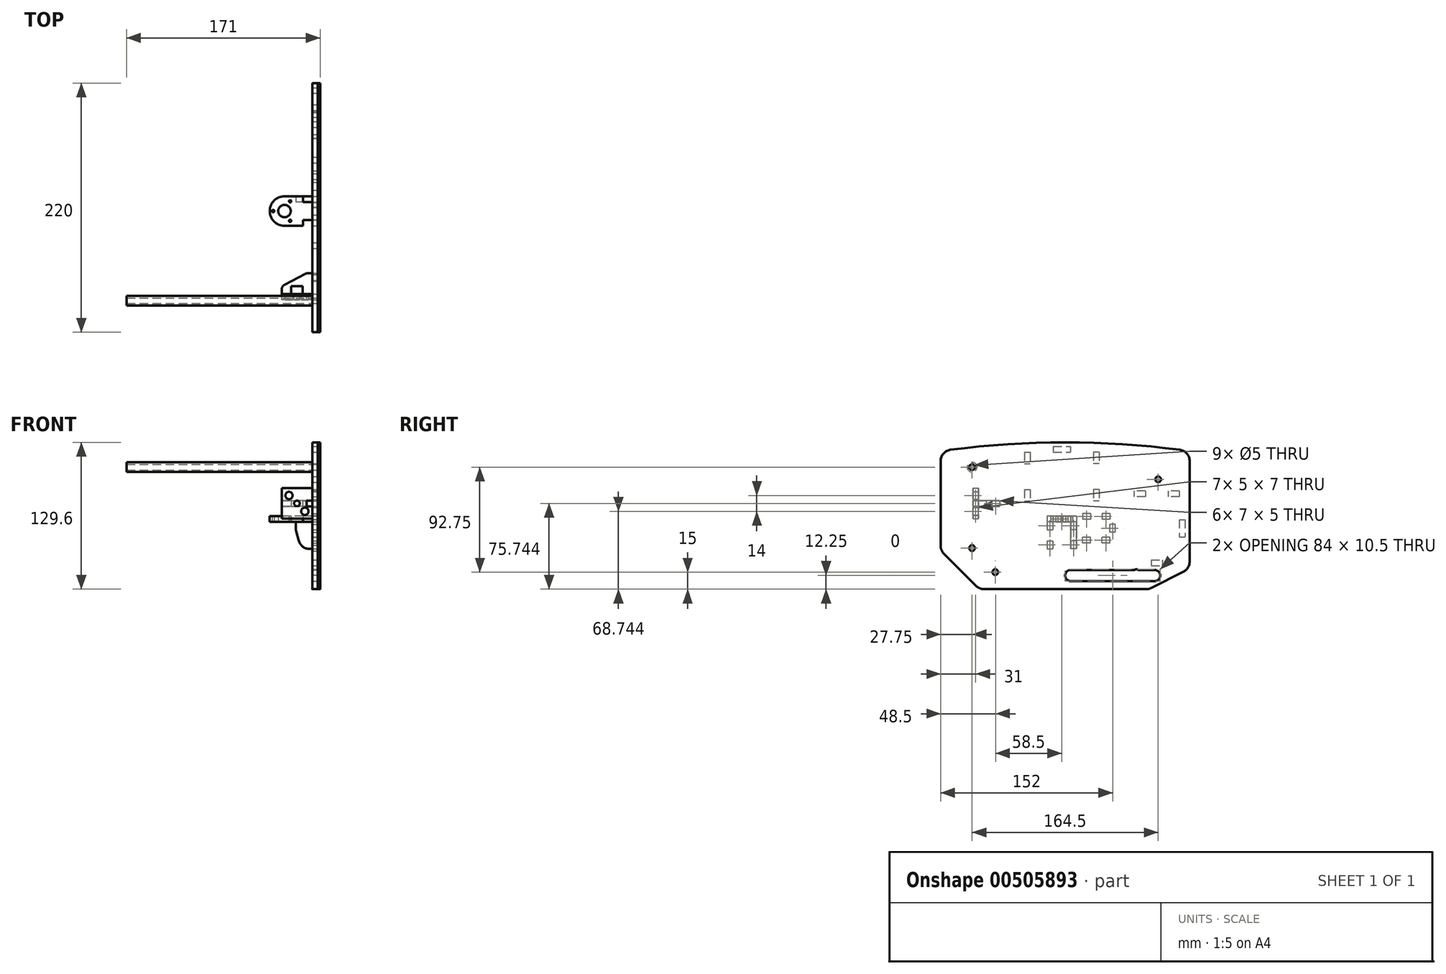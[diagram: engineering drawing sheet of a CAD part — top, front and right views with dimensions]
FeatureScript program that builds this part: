
annotation { "Feature Type Name" : "Feature", "Feature Type Description" : "" }
export const myFeature = defineFeature(function(context is Context, id is Id, definition is map)
    precondition{}
    {
        {
            var Q0;
            Q0=qCreatedBy(makeId("Right.planeOp"),FACE);
            var sketch = newSketch(context, id + "F0", { "sketchPlane" : qUnion([Q0])});
            skLineSegment(sketch, "E0", {"start": v(-71.74, 0) * mm, "end": v(71.74, 0) * mm});
            skLineSegment(sketch, "E1", {"start": v(-78.81, 2.93) * mm, "end": v(-107.07, 31.17) * mm});
            skLineSegment(sketch, "E2", {"start": v(-110, 38.24) * mm, "end": v(-110, 113.24) * mm});
            skLineSegment(sketch, "E3", {"start": v(76.24, 1.07) * mm, "end": v(104.5, 15.31) * mm});
            skLineSegment(sketch, "E4", {"start": v(110, 24.24) * mm, "end": v(110, 113.24) * mm});
            skArc(sketch, "E5", {"start": v(-101.27, 123.16) * mm, "mid": v(0, 129.6) * mm, "end": v(101.27, 123.16) * mm});
            skPoint(sketch, "E6.visualSharp", {"position": v(-110, 122) * mm});
            skArc(sketch, "E6.filletArc", {"start": v(-101.27, 123.16) * mm, "mid": v(-107.5, 119.85) * mm, "end": v(-110, 113.24) * mm});
            skPoint(sketch, "E7.visualSharp", {"position": v(-110, 34.1) * mm});
            skArc(sketch, "E7.filletArc", {"start": v(-110, 38.24) * mm, "mid": v(-109.24, 34.42) * mm, "end": v(-107.07, 31.17) * mm});
            skPoint(sketch, "E8.visualSharp", {"position": v(-75.88, 0) * mm});
            skArc(sketch, "E8.filletArc", {"start": v(-78.81, 2.93) * mm, "mid": v(-75.57, 0.76) * mm, "end": v(-71.74, 0) * mm});
            skPoint(sketch, "E9.visualSharp", {"position": v(74.12, 0) * mm});
            skArc(sketch, "E9.filletArc", {"start": v(71.74, 0) * mm, "mid": v(74.05, 0.27) * mm, "end": v(76.24, 1.07) * mm});
            skPoint(sketch, "E10.visualSharp", {"position": v(110, 18.09) * mm});
            skArc(sketch, "E10.filletArc", {"start": v(104.5, 15.31) * mm, "mid": v(108.51, 19) * mm, "end": v(110, 24.24) * mm});
            skPoint(sketch, "E11.visualSharp", {"position": v(110, 122) * mm});
            skArc(sketch, "E11.filletArc", {"start": v(110, 113.24) * mm, "mid": v(107.5, 119.85) * mm, "end": v(101.27, 123.16) * mm});
            skSolve(sketch);
        }
        {
            var Q0;
            Q0 = qSketchRegion(id + "F0", true);
            extrude(context, id + "F1", {"entities" : qUnion([Q0]), "depth" : 5 * mm});
        }
        {
            var Q0;
            Q0=makeQuery(id+"F1.opExtrude","CAP_FACE",FACE,{"disambiguationData":[OSD([sQuery(id+"F0.wireOp",EDGE,"E0"),sQuery(id+"F0.wireOp",EDGE,"E1"),sQuery(id+"F0.wireOp",EDGE,"E2"),sQuery(id+"F0.wireOp",EDGE,"E3"),sQuery(id+"F0.wireOp",EDGE,"E4"),sQuery(id+"F0.wireOp",EDGE,"E5"),sQuery(id+"F0.wireOp",EDGE,"E6.filletArc"),sQuery(id+"F0.wireOp",EDGE,"E7.filletArc"),sQuery(id+"F0.wireOp",EDGE,"E8.filletArc"),sQuery(id+"F0.wireOp",EDGE,"E9.filletArc"),sQuery(id+"F0.wireOp",EDGE,"E10.filletArc"),sQuery(id+"F0.wireOp",EDGE,"E11.filletArc")])],"isStart":false});
            var sketch = newSketch(context, id + "F2", { "sketchPlane" : qUnion([Q0])});
            skLineSegment(sketch, "E12.bottom", {"start": v(-6.5, 64.5) * mm, "end": v(0.5, 64.5) * mm});
            skLineSegment(sketch, "E12.top", {"start": v(-6.5, 59.5) * mm, "end": v(0.5, 59.5) * mm});
            skLineSegment(sketch, "E12.left", {"start": v(-6.5, 64.5) * mm, "end": v(-6.5, 59.5) * mm});
            skLineSegment(sketch, "E12.right", {"start": v(0.5, 64.5) * mm, "end": v(0.5, 59.5) * mm});
            skPoint(sketch, "E12.middle", {"position": v(-3, 62) * mm});
            skLineSegment(sketch, "E13.bottom", {"start": v(-16, 59.5) * mm, "end": v(-11, 59.5) * mm});
            skLineSegment(sketch, "E13.top", {"start": v(-16, 52.5) * mm, "end": v(-11, 52.5) * mm});
            skLineSegment(sketch, "E13.left", {"start": v(-16, 59.5) * mm, "end": v(-16, 52.5) * mm});
            skLineSegment(sketch, "E13.right", {"start": v(-11, 59.5) * mm, "end": v(-11, 52.5) * mm});
            skLineSegment(sketch, "E14.bottom", {"start": v(-16, 42.5) * mm, "end": v(-11, 42.5) * mm});
            skLineSegment(sketch, "E14.top", {"start": v(-16, 35.5) * mm, "end": v(-11, 35.5) * mm});
            skLineSegment(sketch, "E14.left", {"start": v(-16, 42.5) * mm, "end": v(-16, 35.5) * mm});
            skLineSegment(sketch, "E14.right", {"start": v(-11, 42.5) * mm, "end": v(-11, 35.5) * mm});
            skLineSegment(sketch, "E15", {"start": v(-3, 62) * mm, "end": v(-3, 41.37) * mm, "construction": true});
            skLineSegment(sketch, "E16.MirrorCS", {"start": v(5, 59.5) * mm, "end": v(5, 52.5) * mm});
            skLineSegment(sketch, "E17.MirrorCS", {"start": v(10, 59.5) * mm, "end": v(5, 59.5) * mm});
            skLineSegment(sketch, "E18.MirrorCS", {"start": v(10, 59.5) * mm, "end": v(10, 52.5) * mm});
            skLineSegment(sketch, "E19.MirrorCS", {"start": v(10, 52.5) * mm, "end": v(5, 52.5) * mm});
            skLineSegment(sketch, "E20.MirrorCS", {"start": v(10, 42.5) * mm, "end": v(5, 42.5) * mm});
            skLineSegment(sketch, "E21.MirrorCS", {"start": v(10, 42.5) * mm, "end": v(10, 35.5) * mm});
            skLineSegment(sketch, "E22.MirrorCS", {"start": v(10, 35.5) * mm, "end": v(5, 35.5) * mm});
            skLineSegment(sketch, "E23.MirrorCS", {"start": v(5, 42.5) * mm, "end": v(5, 35.5) * mm});
            skLineSegment(sketch, "E24.bottom", {"start": v(44.5, 50.24) * mm, "end": v(39.5, 50.24) * mm});
            skLineSegment(sketch, "E24.top", {"start": v(44.5, 57.24) * mm, "end": v(39.5, 57.24) * mm});
            skLineSegment(sketch, "E24.left", {"start": v(44.5, 50.24) * mm, "end": v(44.5, 57.24) * mm});
            skLineSegment(sketch, "E24.right", {"start": v(39.5, 50.24) * mm, "end": v(39.5, 57.24) * mm});
            skPoint(sketch, "E24.middle", {"position": v(42, 53.74) * mm});
            skLineSegment(sketch, "E25.bottom", {"start": v(39.5, 66.74) * mm, "end": v(32.5, 66.74) * mm});
            skLineSegment(sketch, "E25.top", {"start": v(39.5, 61.74) * mm, "end": v(32.5, 61.74) * mm});
            skLineSegment(sketch, "E25.left", {"start": v(39.5, 66.74) * mm, "end": v(39.5, 61.74) * mm});
            skLineSegment(sketch, "E25.right", {"start": v(32.5, 66.74) * mm, "end": v(32.5, 61.74) * mm});
            skLineSegment(sketch, "E26.bottom", {"start": v(22.5, 66.74) * mm, "end": v(15.5, 66.74) * mm});
            skLineSegment(sketch, "E26.top", {"start": v(22.5, 61.74) * mm, "end": v(15.5, 61.74) * mm});
            skLineSegment(sketch, "E26.left", {"start": v(22.5, 66.74) * mm, "end": v(22.5, 61.74) * mm});
            skLineSegment(sketch, "E26.right", {"start": v(15.5, 66.74) * mm, "end": v(15.5, 61.74) * mm});
            skLineSegment(sketch, "E27", {"start": v(42, 53.74) * mm, "end": v(21.2, 53.74) * mm, "construction": true});
            skLineSegment(sketch, "E28.MirrorCS", {"start": v(39.5, 45.74) * mm, "end": v(32.5, 45.74) * mm});
            skLineSegment(sketch, "E29.MirrorCS", {"start": v(39.5, 40.74) * mm, "end": v(39.5, 45.74) * mm});
            skLineSegment(sketch, "E30.MirrorCS", {"start": v(39.5, 40.74) * mm, "end": v(32.5, 40.74) * mm});
            skLineSegment(sketch, "E31.MirrorCS", {"start": v(32.5, 40.74) * mm, "end": v(32.5, 45.74) * mm});
            skLineSegment(sketch, "E32.MirrorCS", {"start": v(22.5, 40.74) * mm, "end": v(22.5, 45.74) * mm});
            skLineSegment(sketch, "E33.MirrorCS", {"start": v(22.5, 40.74) * mm, "end": v(15.5, 40.74) * mm});
            skLineSegment(sketch, "E34.MirrorCS", {"start": v(15.5, 40.74) * mm, "end": v(15.5, 45.74) * mm});
            skLineSegment(sketch, "E35.MirrorCS", {"start": v(22.5, 45.74) * mm, "end": v(15.5, 45.74) * mm});
            skPoint(sketch, "E36", {"position": v(-110, 75.74) * mm});
            skCircle(sketch, "E37", {"center": v(5, 12) * mm, "radius": 5 * mm});
            skCircle(sketch, "E38", {"center": v(79, 12) * mm, "radius": 5 * mm});
            skSolve(sketch);
        }
        {
            var Q0;
            Q0 = qSketchRegion(id + "F2", true);
            extrude(context, id + "F3", {"entities" : qUnion([Q0]), "operationType" : NewBodyOperationType.REMOVE, "oppositeDirection" : true, "depth" : 25 * mm});
        }
        {
            var Q0;
            Q0=makeQuery(id+"F1.opExtrude","CAP_FACE",FACE,{"disambiguationData":[OSD([sQuery(id+"F0.wireOp",EDGE,"E0"),sQuery(id+"F0.wireOp",EDGE,"E1"),sQuery(id+"F0.wireOp",EDGE,"E2"),sQuery(id+"F0.wireOp",EDGE,"E3"),sQuery(id+"F0.wireOp",EDGE,"E4"),sQuery(id+"F0.wireOp",EDGE,"E5"),sQuery(id+"F0.wireOp",EDGE,"E6.filletArc"),sQuery(id+"F0.wireOp",EDGE,"E7.filletArc"),sQuery(id+"F0.wireOp",EDGE,"E8.filletArc"),sQuery(id+"F0.wireOp",EDGE,"E9.filletArc"),sQuery(id+"F0.wireOp",EDGE,"E10.filletArc"),sQuery(id+"F0.wireOp",EDGE,"E11.filletArc")])],"isStart":false});
            var sketch = newSketch(context, id + "F4", { "sketchPlane" : qUnion([Q0])});
            skLineSegment(sketch, "E39.bottom", {"start": v(-10.5, 126) * mm, "end": v(4.5, 126) * mm});
            skLineSegment(sketch, "E39.top", {"start": v(-10.5, 121) * mm, "end": v(4.5, 121) * mm});
            skLineSegment(sketch, "E39.left", {"start": v(-10.5, 126) * mm, "end": v(-10.5, 121) * mm});
            skLineSegment(sketch, "E39.right", {"start": v(4.5, 126) * mm, "end": v(4.5, 121) * mm});
            skPoint(sketch, "E39.middle", {"position": v(-3, 123.5) * mm});
            skLineSegment(sketch, "E40.bottom", {"start": v(-36, 121) * mm, "end": v(-31, 121) * mm});
            skLineSegment(sketch, "E40.top", {"start": v(-36, 111) * mm, "end": v(-31, 111) * mm});
            skLineSegment(sketch, "E40.left", {"start": v(-36, 121) * mm, "end": v(-36, 111) * mm});
            skLineSegment(sketch, "E40.right", {"start": v(-31, 121) * mm, "end": v(-31, 111) * mm});
            skLineSegment(sketch, "E41.bottom", {"start": v(-36, 88) * mm, "end": v(-31, 88) * mm});
            skLineSegment(sketch, "E41.top", {"start": v(-36, 78) * mm, "end": v(-31, 78) * mm});
            skLineSegment(sketch, "E41.left", {"start": v(-36, 88) * mm, "end": v(-36, 78) * mm});
            skLineSegment(sketch, "E41.right", {"start": v(-31, 88) * mm, "end": v(-31, 78) * mm});
            skLineSegment(sketch, "E42", {"start": v(-3, 123.5) * mm, "end": v(-3, 101.24) * mm, "construction": true});
            skLineSegment(sketch, "E43.MirrorCS", {"start": v(25, 121) * mm, "end": v(25, 111) * mm});
            skLineSegment(sketch, "E44.MirrorCS", {"start": v(30, 121) * mm, "end": v(25, 121) * mm});
            skLineSegment(sketch, "E45.MirrorCS", {"start": v(30, 121) * mm, "end": v(30, 111) * mm});
            skLineSegment(sketch, "E46.MirrorCS", {"start": v(30, 111) * mm, "end": v(25, 111) * mm});
            skLineSegment(sketch, "E47.MirrorCS", {"start": v(30, 88) * mm, "end": v(25, 88) * mm});
            skLineSegment(sketch, "E48.MirrorCS", {"start": v(30, 88) * mm, "end": v(30, 78) * mm});
            skLineSegment(sketch, "E49.MirrorCS", {"start": v(30, 78) * mm, "end": v(25, 78) * mm});
            skLineSegment(sketch, "E50.MirrorCS", {"start": v(25, 88) * mm, "end": v(25, 78) * mm});
            skLineSegment(sketch, "E51.bottom", {"start": v(101, 61.24) * mm, "end": v(106, 61.24) * mm});
            skLineSegment(sketch, "E51.top", {"start": v(101, 46.24) * mm, "end": v(106, 46.24) * mm});
            skLineSegment(sketch, "E51.left", {"start": v(101, 61.24) * mm, "end": v(101, 46.24) * mm});
            skLineSegment(sketch, "E51.right", {"start": v(106, 61.24) * mm, "end": v(106, 46.24) * mm});
            skPoint(sketch, "E51.middle", {"position": v(103.5, 53.74) * mm});
            skLineSegment(sketch, "E52.bottom", {"start": v(101, 86.74) * mm, "end": v(91, 86.74) * mm});
            skLineSegment(sketch, "E52.top", {"start": v(101, 81.74) * mm, "end": v(91, 81.74) * mm});
            skLineSegment(sketch, "E52.left", {"start": v(101, 86.74) * mm, "end": v(101, 81.74) * mm});
            skLineSegment(sketch, "E52.right", {"start": v(91, 86.74) * mm, "end": v(91, 81.74) * mm});
            skLineSegment(sketch, "E53.bottom", {"start": v(71, 86.74) * mm, "end": v(61, 86.74) * mm});
            skLineSegment(sketch, "E53.top", {"start": v(71, 81.74) * mm, "end": v(61, 81.74) * mm});
            skLineSegment(sketch, "E53.left", {"start": v(71, 86.74) * mm, "end": v(71, 81.74) * mm});
            skLineSegment(sketch, "E53.right", {"start": v(61, 86.74) * mm, "end": v(61, 81.74) * mm});
            skLineSegment(sketch, "E54.bottom", {"start": v(76, 25.74) * mm, "end": v(86, 25.74) * mm});
            skLineSegment(sketch, "E54.top", {"start": v(76, 20.74) * mm, "end": v(86, 20.74) * mm});
            skLineSegment(sketch, "E54.left", {"start": v(86, 25.74) * mm, "end": v(86, 20.74) * mm});
            skLineSegment(sketch, "E54.right", {"start": v(76, 25.74) * mm, "end": v(76, 20.74) * mm});
            skSolve(sketch);
        }
        {
            var Q0;
            Q0 = qSketchRegion(id + "F4", true);
            extrude(context, id + "F5", {"entities" : qUnion([Q0]), "operationType" : NewBodyOperationType.REMOVE, "oppositeDirection" : true, "depth" : 25 * mm});
        }
        {
            var Q0;
            Q0=makeQuery(id+"F1.opExtrude","CAP_FACE",FACE,{"disambiguationData":[OSD([sQuery(id+"F0.wireOp",EDGE,"E0"),sQuery(id+"F0.wireOp",EDGE,"E1"),sQuery(id+"F0.wireOp",EDGE,"E2"),sQuery(id+"F0.wireOp",EDGE,"E3"),sQuery(id+"F0.wireOp",EDGE,"E4"),sQuery(id+"F0.wireOp",EDGE,"E5"),sQuery(id+"F0.wireOp",EDGE,"E6.filletArc"),sQuery(id+"F0.wireOp",EDGE,"E7.filletArc"),sQuery(id+"F0.wireOp",EDGE,"E8.filletArc"),sQuery(id+"F0.wireOp",EDGE,"E9.filletArc"),sQuery(id+"F0.wireOp",EDGE,"E10.filletArc"),sQuery(id+"F0.wireOp",EDGE,"E11.filletArc")])],"isStart":false});
            var sketch = newSketch(context, id + "F6", { "sketchPlane" : qUnion([Q0])});
            skLineSegment(sketch, "E55.bottom", {"start": v(-108.5, 89.24) * mm, "end": v(-81.5, 89.24) * mm, "construction": true});
            skLineSegment(sketch, "E55.top", {"start": v(-108.5, 62.24) * mm, "end": v(-81.5, 62.24) * mm, "construction": true});
            skLineSegment(sketch, "E55.left", {"start": v(-108.5, 89.24) * mm, "end": v(-108.5, 62.24) * mm, "construction": true});
            skLineSegment(sketch, "E55.right", {"start": v(-81.5, 89.24) * mm, "end": v(-81.5, 62.24) * mm, "construction": true});
            skPoint(sketch, "E55.middle", {"position": v(-95, 75.74) * mm});
            skLineSegment(sketch, "E56.bottom", {"start": v(-65, 78.24) * mm, "end": v(-58, 78.24) * mm});
            skLineSegment(sketch, "E56.top", {"start": v(-65, 73.24) * mm, "end": v(-58, 73.24) * mm});
            skLineSegment(sketch, "E56.left", {"start": v(-65, 78.24) * mm, "end": v(-65, 73.24) * mm});
            skLineSegment(sketch, "E56.right", {"start": v(-58, 78.24) * mm, "end": v(-58, 73.24) * mm});
            skPoint(sketch, "E56.middle", {"position": v(-61.5, 75.74) * mm});
            skLineSegment(sketch, "E57.bottom", {"start": v(-81.5, 86.24) * mm, "end": v(-76.5, 86.24) * mm});
            skLineSegment(sketch, "E57.top", {"start": v(-81.5, 79.24) * mm, "end": v(-76.5, 79.24) * mm});
            skLineSegment(sketch, "E57.left", {"start": v(-81.5, 86.24) * mm, "end": v(-81.5, 79.24) * mm});
            skLineSegment(sketch, "E57.right", {"start": v(-76.5, 86.24) * mm, "end": v(-76.5, 79.24) * mm});
            skLineSegment(sketch, "E58.bottom", {"start": v(-81.5, 65.24) * mm, "end": v(-76.5, 65.24) * mm});
            skLineSegment(sketch, "E58.top", {"start": v(-81.5, 72.24) * mm, "end": v(-76.5, 72.24) * mm});
            skLineSegment(sketch, "E58.left", {"start": v(-81.5, 65.24) * mm, "end": v(-81.5, 72.24) * mm});
            skLineSegment(sketch, "E58.right", {"start": v(-76.5, 65.24) * mm, "end": v(-76.5, 72.24) * mm});
            skLineSegment(sketch, "E59", {"start": v(-95, 75.74) * mm, "end": v(-61.5, 75.74) * mm, "construction": true});
            skSolve(sketch);
        }
        {
            var Q0;
            Q0 = qSketchRegion(id + "F6", true);
            extrude(context, id + "F7", {"entities" : qUnion([Q0]), "operationType" : NewBodyOperationType.REMOVE, "oppositeDirection" : true, "depth" : 25 * mm});
        }
        {
            var Q0;
            Q0=makeQuery(id+"F3.boolean.opBoolean","COPY",FACE,{"derivedFrom":makeQuery(id+"F3.opExtrude","SWEPT_FACE",FACE,{"disambiguationData":[OSD([sQuery(id+"F2.wireOp",EDGE,"E12.top")])]})});
            var sketch = newSketch(context, id + "F8", { "sketchPlane" : qUnion([Q0])});
            skCircle(sketch, "E60", {"center": v(-24.5, -3) * mm, "radius": 13 * mm});
            skLineSegment(sketch, "E61.0", {"start": v(0, 0.5) * mm, "end": v(5, 0.5) * mm});
            skLineSegment(sketch, "E61.1", {"start": v(5, -6.5) * mm, "end": v(5, 0.5) * mm});
            skLineSegment(sketch, "E61.2", {"start": v(0, -6.5) * mm, "end": v(5, -6.5) * mm});
            skLineSegment(sketch, "E62", {"start": v(0, 0.5) * mm, "end": v(0, 5) * mm});
            skLineSegment(sketch, "E63", {"start": v(0, -6.5) * mm, "end": v(0, -11) * mm});
            skLineSegment(sketch, "E64", {"start": v(0, 5) * mm, "end": v(-8, 5) * mm});
            skLineSegment(sketch, "E65", {"start": v(-8, 5) * mm, "end": v(-8, 10) * mm});
            skLineSegment(sketch, "E66", {"start": v(0, -11) * mm, "end": v(-8, -11) * mm});
            skLineSegment(sketch, "E67", {"start": v(-8, -11) * mm, "end": v(-8, -16) * mm});
            skPoint(sketch, "E68", {"position": v(5, -3) * mm});
            skLineSegment(sketch, "E69", {"start": v(-8, 10) * mm, "end": v(-24.5, 10) * mm});
            skLineSegment(sketch, "E70", {"start": v(-8, -16) * mm, "end": v(-24.5, -16) * mm});
            skCircle(sketch, "E71", {"center": v(-24.5, -3) * mm, "radius": 22.5 * mm, "construction": true});
            skCircle(sketch, "E72", {"center": v(-24.5, -3) * mm, "radius": 5.5 * mm});
            skCircle(sketch, "E73", {"center": v(-34.5, -3) * mm, "radius": 1 * mm});
            skCircle(sketch, "E74.1.0", {"center": v(-19.5, -11.66) * mm, "radius": 1 * mm});
            skCircle(sketch, "E74.2.0", {"center": v(-19.5, 5.66) * mm, "radius": 1 * mm});
            skSolve(sketch);
        }
        {
            var Q0;
            Q0 = qSketchRegion(id + "F8", true);
            extrude(context, id + "F9", {"entities" : qUnion([Q0]), "depth" : 5 * mm});
        }
        {
            var Q0;
            Q0=makeQuery(id+"F9.opExtrude","SWEPT_FACE",FACE,{"disambiguationData":[OSD([sQuery(id+"F8.wireOp",EDGE,"E64")])]});
            var sketch = newSketch(context, id + "F10", { "sketchPlane" : qUnion([Q0])});
            skLineSegment(sketch, "E75.0", {"start": v(0, 59.5) * mm, "end": v(-5, 59.5) * mm});
            skLineSegment(sketch, "E75.1", {"start": v(-5, 59.5) * mm, "end": v(-5, 52.5) * mm});
            skLineSegment(sketch, "E75.2", {"start": v(0, 52.5) * mm, "end": v(-5, 52.5) * mm});
            skLineSegment(sketch, "E76.0", {"start": v(0, 64.5) * mm, "end": v(0, 59.5) * mm});
            skLineSegment(sketch, "E76.1", {"start": v(0, 64.5) * mm, "end": v(8, 64.5) * mm});
            skLineSegment(sketch, "E76.2", {"start": v(8, 64.5) * mm, "end": v(8, 59.5) * mm});
            skLineSegment(sketch, "E77", {"start": v(8, 59.5) * mm, "end": v(14.5, 59.5) * mm});
            skLineSegment(sketch, "E78.0", {"start": v(0, 42.5) * mm, "end": v(-5, 42.5) * mm});
            skLineSegment(sketch, "E78.1", {"start": v(-5, 42.5) * mm, "end": v(-5, 35.5) * mm});
            skLineSegment(sketch, "E78.2", {"start": v(0, 35.5) * mm, "end": v(-5, 35.5) * mm});
            skLineSegment(sketch, "E79", {"start": v(0, 52.5) * mm, "end": v(0, 42.5) * mm});
            skLineSegment(sketch, "E80", {"start": v(0, 35.5) * mm, "end": v(2.3, 35.5) * mm});
            skLineSegment(sketch, "E81", {"start": v(11.97, 42.94) * mm, "end": v(14.17, 51.24) * mm});
            skLineSegment(sketch, "E82", {"start": v(14.5, 53.8) * mm, "end": v(14.5, 59.5) * mm});
            skLineSegment(sketch, "E83.0", {"start": v(18.5, 64.5) * mm, "end": v(20.5, 64.5) * mm, "construction": true});
            skPoint(sketch, "E84.visualSharp", {"position": v(10, 35.5) * mm});
            skArc(sketch, "E84.filletArc", {"start": v(2.3, 35.5) * mm, "mid": v(8.4, 37.58) * mm, "end": v(11.97, 42.94) * mm});
            skPoint(sketch, "E85.visualSharp", {"position": v(14.5, 52.5) * mm});
            skArc(sketch, "E85.filletArc", {"start": v(14.17, 51.24) * mm, "mid": v(14.42, 52.51) * mm, "end": v(14.5, 53.8) * mm});
            skSolve(sketch);
        }
        {
            var Q0;
            Q0 = qSketchRegion(id + "F10", true);
            extrude(context, id + "F11", {"entities" : qUnion([Q0]), "depth" : 5 * mm});
        }
        {
            var Q0;
            Q0=makeQuery(id+"F7.boolean.opBoolean","COPY",FACE,{"derivedFrom":makeQuery(id+"F7.opExtrude","SWEPT_FACE",FACE,{"disambiguationData":[OSD([sQuery(id+"F6.wireOp",EDGE,"E57.right")])]})});
            var sketch = newSketch(context, id + "F12", { "sketchPlane" : qUnion([Q0])});
            skLineSegment(sketch, "E86.0", {"start": v(0, 86.24) * mm, "end": v(5, 86.24) * mm});
            skLineSegment(sketch, "E86.1", {"start": v(5, 86.24) * mm, "end": v(5, 79.24) * mm});
            skLineSegment(sketch, "E86.2", {"start": v(0, 79.24) * mm, "end": v(5, 79.24) * mm});
            skLineSegment(sketch, "E86.3", {"start": v(0, 72.24) * mm, "end": v(5, 72.24) * mm});
            skLineSegment(sketch, "E86.4", {"start": v(5, 65.24) * mm, "end": v(5, 72.24) * mm});
            skLineSegment(sketch, "E86.5", {"start": v(0, 65.24) * mm, "end": v(5, 65.24) * mm});
            skLineSegment(sketch, "E87", {"start": v(0, 79.24) * mm, "end": v(0, 72.24) * mm});
            skLineSegment(sketch, "E88", {"start": v(0, 86.24) * mm, "end": v(0, 89.24) * mm});
            skLineSegment(sketch, "E89", {"start": v(0, 89.24) * mm, "end": v(-27, 89.24) * mm});
            skLineSegment(sketch, "E90", {"start": v(-27, 89.24) * mm, "end": v(-27, 62.24) * mm});
            skLineSegment(sketch, "E91", {"start": v(-27, 62.24) * mm, "end": v(0, 62.24) * mm});
            skLineSegment(sketch, "E92", {"start": v(0, 62.24) * mm, "end": v(0, 65.24) * mm});
            skLineSegment(sketch, "E93", {"start": v(-27, 89.24) * mm, "end": v(0, 62.24) * mm, "construction": true});
            skPoint(sketch, "E94", {"position": v(-13.5, 75.74) * mm});
            skPoint(sketch, "E95", {"position": v(0, 75.74) * mm});
            skCircle(sketch, "E96", {"center": v(-13.5, 75.74) * mm, "radius": 2.5 * mm});
            skCircle(sketch, "E97", {"center": v(-20.5, 82.74) * mm, "radius": 3.25 * mm});
            skCircle(sketch, "E98", {"center": v(-6.5, 68.74) * mm, "radius": 3.25 * mm});
            skLineSegment(sketch, "E99.bottom", {"start": v(0, 78.24) * mm, "end": v(-5, 78.24) * mm});
            skLineSegment(sketch, "E99.top", {"start": v(0, 73.24) * mm, "end": v(-5, 73.24) * mm});
            skLineSegment(sketch, "E99.left", {"start": v(0, 78.24) * mm, "end": v(0, 73.24) * mm});
            skLineSegment(sketch, "E99.right", {"start": v(-5, 78.24) * mm, "end": v(-5, 73.24) * mm});
            skPoint(sketch, "E99.middle", {"position": v(-2.5, 75.74) * mm});
            skSolve(sketch);
        }
        {
            var Q0;
            Q0=makeQuery(id+"F12.imprint","IMPRINT",FACE,{"disambiguationData":[TD([[makeQuery(id+"F12.imprint","IMPRINT",EDGE,{"derivedFrom":sQuery(id+"F12.wireOp",EDGE,"E86.0")}),-1.0]])]});
            var Q1;
            {var subQ1=sQuery(id+"F12.wireOp",EDGE,"E86.3");Q1=makeQuery(id+"F12.imprint","IMPRINT",FACE,{"disambiguationData":[TD([[makeQuery(id+"F12.imprint","IMPRINT",EDGE,{"derivedFrom":subQ1}),-1.0]])]});}
            extrude(context, id + "F13", {"entities" : qUnion([Q0, Q1]), "depth" : 5 * mm});
        }
        {
            var Q0;
            Q0=makeQuery(id+"F7.boolean.opBoolean","COPY",FACE,{"derivedFrom":makeQuery(id+"F7.opExtrude","SWEPT_FACE",FACE,{"disambiguationData":[OSD([sQuery(id+"F6.wireOp",EDGE,"E56.top")])]})});
            var sketch = newSketch(context, id + "F14", { "sketchPlane" : qUnion([Q0])});
            skLineSegment(sketch, "E100.0", {"start": v(0, -58) * mm, "end": v(5, -58) * mm});
            skLineSegment(sketch, "E100.1", {"start": v(5, -65) * mm, "end": v(5, -58) * mm});
            skLineSegment(sketch, "E100.2", {"start": v(0, -65) * mm, "end": v(5, -65) * mm});
            skLineSegment(sketch, "E101.0", {"start": v(0, -81.5) * mm, "end": v(0, -76.5) * mm});
            skLineSegment(sketch, "E101.1", {"start": v(0, -81.5) * mm, "end": v(-5, -81.5) * mm});
            skLineSegment(sketch, "E101.2", {"start": v(-5, -81.5) * mm, "end": v(-5, -76.5) * mm});
            skLineSegment(sketch, "E102", {"start": v(0, -65) * mm, "end": v(0, -76.5) * mm});
            skLineSegment(sketch, "E103", {"start": v(0, -58) * mm, "end": v(-3.77, -58) * mm});
            skLineSegment(sketch, "E104", {"start": v(-6.09, -58.57) * mm, "end": v(-24.32, -68.1) * mm});
            skLineSegment(sketch, "E105", {"start": v(-27, -72.53) * mm, "end": v(-27, -76.5) * mm});
            skLineSegment(sketch, "E106", {"start": v(-27, -76.5) * mm, "end": v(-18.5, -76.5) * mm});
            skLineSegment(sketch, "E107", {"start": v(-18.5, -76.5) * mm, "end": v(-18.5, -69.5) * mm});
            skLineSegment(sketch, "E108", {"start": v(-18.5, -69.5) * mm, "end": v(-8.5, -69.5) * mm});
            skLineSegment(sketch, "E109", {"start": v(-8.5, -69.5) * mm, "end": v(-8.5, -76.5) * mm});
            skLineSegment(sketch, "E110", {"start": v(-8.5, -76.5) * mm, "end": v(-5, -76.5) * mm});
            skPoint(sketch, "E111.visualSharp", {"position": v(-5, -58) * mm});
            skArc(sketch, "E111.filletArc", {"start": v(-3.77, -58) * mm, "mid": v(-4.96, -58.14) * mm, "end": v(-6.09, -58.57) * mm});
            skPoint(sketch, "E112.visualSharp", {"position": v(-27, -69.5) * mm});
            skArc(sketch, "E112.filletArc", {"start": v(-24.32, -68.1) * mm, "mid": v(-26.28, -69.94) * mm, "end": v(-27, -72.53) * mm});
            skLineSegment(sketch, "E113.0", {"start": v(-11, -81.5) * mm, "end": v(-16, -81.5) * mm, "construction": true});
            skPoint(sketch, "E114", {"position": v(-13.5, -81.5) * mm});
            skPoint(sketch, "E115", {"position": v(-13.5, -69.5) * mm});
            skSolve(sketch);
        }
        {
            var Q0;
            Q0 = qSketchRegion(id + "F14", true);
            extrude(context, id + "F15", {"entities" : qUnion([Q0]), "depth" : 5 * mm});
        }
        {
            var Q0;
            Q0=makeQuery(id+"F1.opExtrude","CAP_FACE",FACE,{"disambiguationData":[OSD([sQuery(id+"F0.wireOp",EDGE,"E0"),sQuery(id+"F0.wireOp",EDGE,"E1"),sQuery(id+"F0.wireOp",EDGE,"E2"),sQuery(id+"F0.wireOp",EDGE,"E3"),sQuery(id+"F0.wireOp",EDGE,"E4"),sQuery(id+"F0.wireOp",EDGE,"E5"),sQuery(id+"F0.wireOp",EDGE,"E6.filletArc"),sQuery(id+"F0.wireOp",EDGE,"E7.filletArc"),sQuery(id+"F0.wireOp",EDGE,"E8.filletArc"),sQuery(id+"F0.wireOp",EDGE,"E9.filletArc"),sQuery(id+"F0.wireOp",EDGE,"E10.filletArc"),sQuery(id+"F0.wireOp",EDGE,"E11.filletArc")])],"isStart":false});
            var sketch = newSketch(context, id + "F16", { "sketchPlane" : qUnion([Q0])});
            skLineSegment(sketch, "E116.0", {"start": v(-71.74, 0) * mm, "end": v(71.74, 0) * mm});
            skLineSegment(sketch, "E116.1", {"start": v(-78.81, 2.93) * mm, "end": v(-107.07, 31.17) * mm});
            skLineSegment(sketch, "E116.2", {"start": v(-110, 38.24) * mm, "end": v(-110, 113.24) * mm});
            skLineSegment(sketch, "E116.3", {"start": v(76.24, 1.07) * mm, "end": v(104.5, 15.31) * mm});
            skLineSegment(sketch, "E116.4", {"start": v(110, 24.24) * mm, "end": v(110, 113.24) * mm});
            skArc(sketch, "E116.5", {"start": v(-101.27, 123.16) * mm, "mid": v(0, 129.6) * mm, "end": v(101.27, 123.16) * mm});
            skPoint(sketch, "E116.6", {"position": v(-110, 122) * mm});
            skArc(sketch, "E116.7", {"start": v(-101.27, 123.16) * mm, "mid": v(-107.5, 119.85) * mm, "end": v(-110, 113.24) * mm});
            skPoint(sketch, "E116.8", {"position": v(-110, 34.1) * mm});
            skArc(sketch, "E116.9", {"start": v(-110, 38.24) * mm, "mid": v(-109.24, 34.42) * mm, "end": v(-107.07, 31.17) * mm});
            skPoint(sketch, "E116.10", {"position": v(-75.88, 0) * mm});
            skArc(sketch, "E116.11", {"start": v(-78.81, 2.93) * mm, "mid": v(-75.57, 0.76) * mm, "end": v(-71.74, 0) * mm});
            skPoint(sketch, "E116.12", {"position": v(74.12, 0) * mm});
            skArc(sketch, "E116.13", {"start": v(71.74, 0) * mm, "mid": v(74.05, 0.27) * mm, "end": v(76.24, 1.07) * mm});
            skPoint(sketch, "E116.14", {"position": v(110, 18.09) * mm});
            skArc(sketch, "E116.15", {"start": v(104.5, 15.31) * mm, "mid": v(108.51, 19) * mm, "end": v(110, 24.24) * mm});
            skPoint(sketch, "E116.16", {"position": v(110, 122) * mm});
            skArc(sketch, "E116.17", {"start": v(110, 113.24) * mm, "mid": v(107.5, 119.85) * mm, "end": v(101.27, 123.16) * mm});
            skSolve(sketch);
        }
        {
            var Q0;
            Q0 = qSketchRegion(id + "F16", true);
            extrude(context, id + "F17", {"entities" : qUnion([Q0]), "depth" : 2 * mm});
        }
        {
            var Q0;
            Q0=makeQuery(id+"F17.opExtrude","CAP_FACE",FACE,{"disambiguationData":[OSD([sQuery(id+"F16.wireOp",EDGE,"E116.0"),sQuery(id+"F16.wireOp",EDGE,"E116.1"),sQuery(id+"F16.wireOp",EDGE,"E116.2"),sQuery(id+"F16.wireOp",EDGE,"E116.3"),sQuery(id+"F16.wireOp",EDGE,"E116.4"),sQuery(id+"F16.wireOp",EDGE,"E116.5"),sQuery(id+"F16.wireOp",EDGE,"E116.7"),sQuery(id+"F16.wireOp",EDGE,"E116.9"),sQuery(id+"F16.wireOp",EDGE,"E116.11"),sQuery(id+"F16.wireOp",EDGE,"E116.13"),sQuery(id+"F16.wireOp",EDGE,"E116.15"),sQuery(id+"F16.wireOp",EDGE,"E116.17")])],"isStart":false});
            var sketch = newSketch(context, id + "F18", { "sketchPlane" : qUnion([Q0])});
            skCircle(sketch, "E117", {"center": v(-82.25, 107.75) * mm, "radius": 2.5 * mm});
            skCircle(sketch, "E118", {"center": v(-82.25, 36.25) * mm, "radius": 2.5 * mm});
            skCircle(sketch, "E119", {"center": v(-61.74, 15) * mm, "radius": 2.5 * mm});
            skCircle(sketch, "E120", {"center": v(62.96, 15) * mm, "radius": 2.5 * mm});
            skCircle(sketch, "E121", {"center": v(82.25, 97) * mm, "radius": 2.5 * mm});
            skCircle(sketch, "E122", {"center": v(-82.25, 107.75) * mm, "radius": 4.25 * mm, "construction": true});
            skCircle(sketch, "E123", {"center": v(-82.25, 36.25) * mm, "radius": 4.25 * mm, "construction": true});
            skCircle(sketch, "E124", {"center": v(82.25, 97) * mm, "radius": 4.25 * mm, "construction": true});
            skLineSegment(sketch, "E125.bottom", {"start": v(-78, 112) * mm, "end": v(78, 112) * mm, "construction": true});
            skLineSegment(sketch, "E125.top", {"start": v(-78, 32) * mm, "end": v(78, 32) * mm, "construction": true});
            skLineSegment(sketch, "E125.left", {"start": v(-78, 112) * mm, "end": v(-78, 32) * mm, "construction": true});
            skLineSegment(sketch, "E125.right", {"start": v(78, 112) * mm, "end": v(78, 32) * mm, "construction": true});
            skPoint(sketch, "E125.middle", {"position": v(0, 72) * mm});
            skCircle(sketch, "E126", {"center": v(-75, 72) * mm, "radius": 30 * mm, "construction": true});
            skLineSegment(sketch, "E127.bottom", {"start": v(-71.74, 25) * mm, "end": v(-51.74, 25) * mm, "construction": true});
            skLineSegment(sketch, "E127.top", {"start": v(-71.74, 5) * mm, "end": v(-51.74, 5) * mm, "construction": true});
            skLineSegment(sketch, "E127.left", {"start": v(-71.74, 25) * mm, "end": v(-71.74, 5) * mm, "construction": true});
            skLineSegment(sketch, "E127.right", {"start": v(-51.74, 25) * mm, "end": v(-51.74, 5) * mm, "construction": true});
            skSolve(sketch);
        }
        {
            var Q0;
            Q0 = qSketchRegion(id + "F18", true);
            extrude(context, id + "F19", {"entities" : qUnion([Q0]), "operationType" : NewBodyOperationType.REMOVE, "oppositeDirection" : true, "depth" : 25 * mm});
        }
        {
            var Q0;
            Q0=makeQuery(id+"F1.opExtrude","CAP_FACE",FACE,{"disambiguationData":[OSD([sQuery(id+"F0.wireOp",EDGE,"E0"),sQuery(id+"F0.wireOp",EDGE,"E1"),sQuery(id+"F0.wireOp",EDGE,"E2"),sQuery(id+"F0.wireOp",EDGE,"E3"),sQuery(id+"F0.wireOp",EDGE,"E4"),sQuery(id+"F0.wireOp",EDGE,"E5"),sQuery(id+"F0.wireOp",EDGE,"E6.filletArc"),sQuery(id+"F0.wireOp",EDGE,"E7.filletArc"),sQuery(id+"F0.wireOp",EDGE,"E8.filletArc"),sQuery(id+"F0.wireOp",EDGE,"E9.filletArc"),sQuery(id+"F0.wireOp",EDGE,"E10.filletArc"),sQuery(id+"F0.wireOp",EDGE,"E11.filletArc")])],"isStart":true});
            var sketch = newSketch(context, id + "F20", { "sketchPlane" : qUnion([Q0])});
            skCircle(sketch, "E128.0", {"center": v(82.25, 107.75) * mm, "radius": 2.5 * mm});
            skCircle(sketch, "E129", {"center": v(82.25, 107.75) * mm, "radius": 4.25 * mm});
            skSolve(sketch);
        }
        {
            var Q0;
            Q0 = qSketchRegion(id + "F20", true);
            extrude(context, id + "F21", {"entities" : qUnion([Q0]), "depth" : 164 * mm});
        }
        {
            var Q0;
            Q0=makeQuery(id+"F17.opExtrude","CAP_FACE",FACE,{"disambiguationData":[OSD([sQuery(id+"F16.wireOp",EDGE,"E116.0"),sQuery(id+"F16.wireOp",EDGE,"E116.1"),sQuery(id+"F16.wireOp",EDGE,"E116.2"),sQuery(id+"F16.wireOp",EDGE,"E116.3"),sQuery(id+"F16.wireOp",EDGE,"E116.4"),sQuery(id+"F16.wireOp",EDGE,"E116.5"),sQuery(id+"F16.wireOp",EDGE,"E116.7"),sQuery(id+"F16.wireOp",EDGE,"E116.9"),sQuery(id+"F16.wireOp",EDGE,"E116.11"),sQuery(id+"F16.wireOp",EDGE,"E116.13"),sQuery(id+"F16.wireOp",EDGE,"E116.15"),sQuery(id+"F16.wireOp",EDGE,"E116.17")])],"isStart":false});
            var sketch = newSketch(context, id + "F22", { "sketchPlane" : qUnion([Q0])});
            skCircle(sketch, "E130.0", {"center": v(79, 12) * mm, "radius": 5 * mm});
            skCircle(sketch, "E130.1", {"center": v(5, 12) * mm, "radius": 5 * mm});
            skLineSegment(sketch, "E131", {"start": v(5, 17) * mm, "end": v(79, 17) * mm});
            skLineSegment(sketch, "E132", {"start": v(5, 7) * mm, "end": v(79, 7) * mm});
            skSolve(sketch);
        }
        {
            var Q0;
            Q0 = qSketchRegion(id + "F22", true);
            extrude(context, id + "F23", {"entities" : qUnion([Q0]), "operationType" : NewBodyOperationType.REMOVE, "oppositeDirection" : true, "depth" : 25 * mm, "offsetDistance" : 25 * mm});
        }
    });
